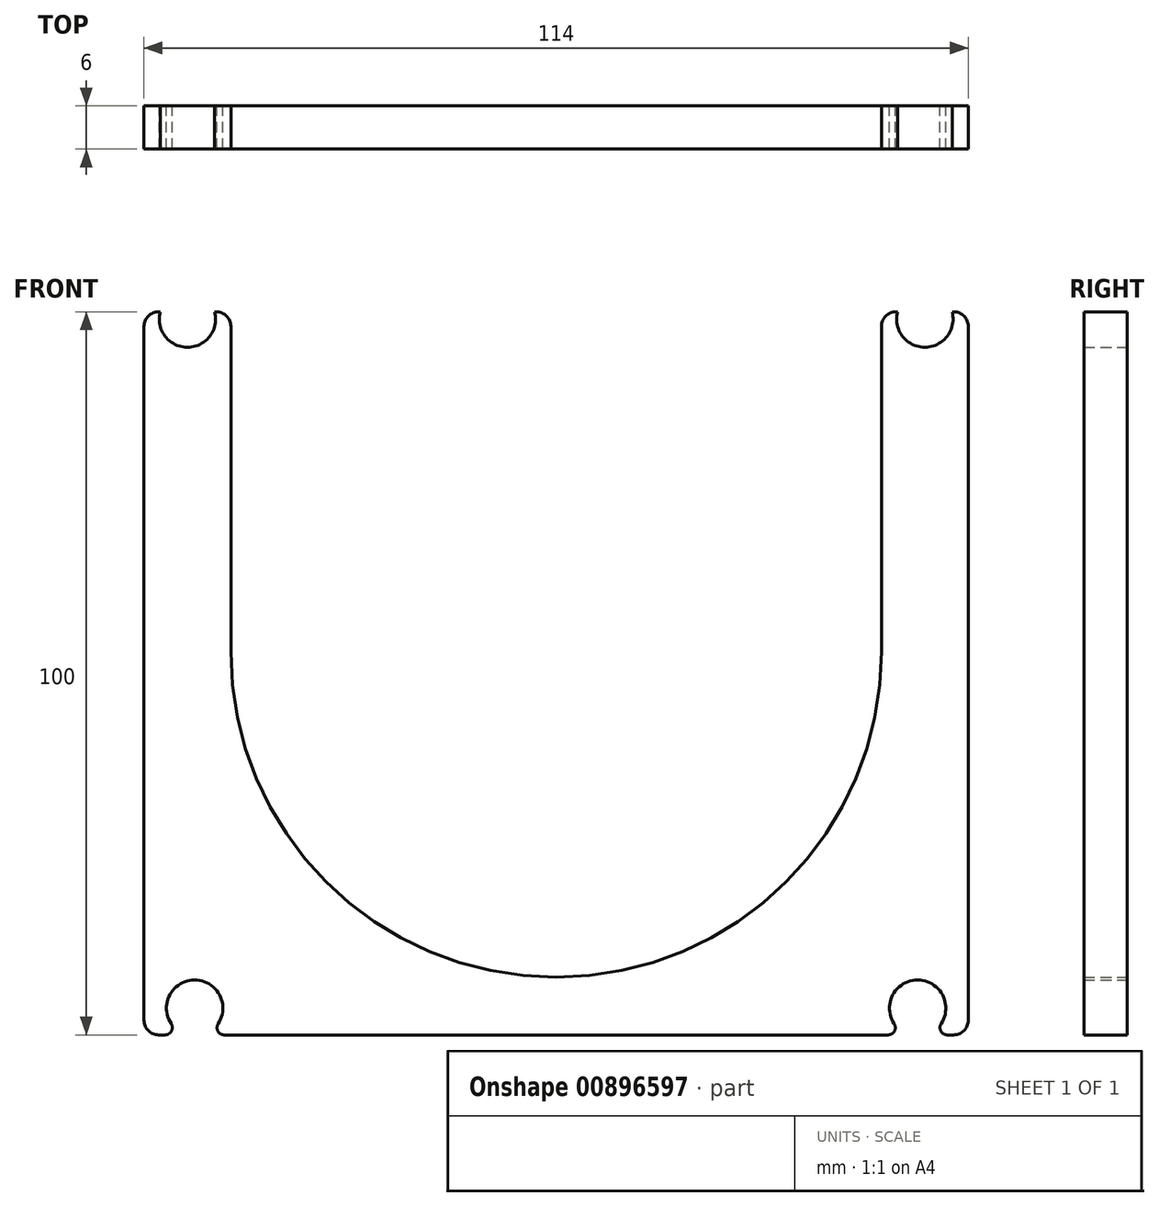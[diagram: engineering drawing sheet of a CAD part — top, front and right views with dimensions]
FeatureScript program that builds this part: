
annotation { "Feature Type Name" : "Feature", "Feature Type Description" : "" }
export const myFeature = defineFeature(function(context is Context, id is Id, definition is map)
    precondition{}
    {
        {
            var Q0;
            Q0=qCreatedBy(makeId("Front.planeOp"),FACE);
            var sketch = newSketch(context, id + "F0", { "sketchPlane" : qUnion([Q0])});
            skArc(sketch, "E0", {"start": v(-45, 53) * mm, "mid": v(0, 8) * mm, "end": v(45, 53) * mm});
            skLineSegment(sketch, "E1.bottom", {"start": v(-57, 100) * mm, "end": v(-54.77, 100) * mm});
            skLineSegment(sketch, "E1.top", {"start": v(-57, 0) * mm, "end": v(57, 0) * mm});
            skLineSegment(sketch, "E1.left", {"start": v(-57, 100) * mm, "end": v(-57, 0) * mm});
            skLineSegment(sketch, "E1.right", {"start": v(57, 100) * mm, "end": v(57, 0) * mm});
            skPoint(sketch, "E2", {"position": v(0, 0) * mm});
            skLineSegment(sketch, "E3", {"start": v(-45, 53) * mm, "end": v(-45, 100) * mm});
            skLineSegment(sketch, "E4.MirrorCS", {"start": v(45, 53) * mm, "end": v(45, 100) * mm});
            skLineSegment(sketch, "E5.trimOffspring", {"start": v(45, 100) * mm, "end": v(47.23, 100) * mm});
            skArc(sketch, "E6", {"start": v(47.23, 100) * mm, "mid": v(51, 95.1) * mm, "end": v(54.77, 100) * mm});
            skPoint(sketch, "E6.centerSnap0", {"position": v(51, 100) * mm});
            skLineSegment(sketch, "E7.trimOffspring", {"start": v(54.77, 100) * mm, "end": v(57, 100) * mm});
            skArc(sketch, "E8.MirrorCS", {"start": v(-47.23, 100) * mm, "mid": v(-51, 95.1) * mm, "end": v(-54.77, 100) * mm});
            skLineSegment(sketch, "E9.trimOffspring", {"start": v(-47.23, 100) * mm, "end": v(-45, 100) * mm});
            skSolve(sketch);
        }
        {
            var Q0;
            Q0 = qSketchRegion(id + "F0", true);
            extrude(context, id + "F1", {"entities" : qUnion([Q0]), "depth" : 6 * mm, "offsetDistance" : 25 * mm});
        }
        {
            var Q0;
            Q0=qCreatedBy(makeId("Front.planeOp"),FACE);
            var sketch = newSketch(context, id + "F2", { "sketchPlane" : qUnion([Q0])});
            skCircle(sketch, "E10", {"center": v(-50, 3.7) * mm, "radius": 3.9 * mm});
            skCircle(sketch, "E11.MirrorC", {"center": v(50, 3.7) * mm, "radius": 3.9 * mm});
            skSolve(sketch);
        }
        {
            var Q0;
            Q0 = qSketchRegion(id + "F2", true);
            extrude(context, id + "F3", {"entities" : qUnion([Q0]), "operationType" : NewBodyOperationType.REMOVE, "endBound" : BoundingType.THROUGH_ALL, "depth" : 25 * mm, "offsetDistance" : 25 * mm});
        }
        {
            var Q0;
            Q0=makeQuery(id+"F1.opExtrude","SWEPT_EDGE",EDGE,{"disambiguationData":[OSD([sQuery(id+"F0.wireOp",EDGE,"E3"),sQuery(id+"F0.wireOp",EDGE,"E9.trimOffspring")])]});
            var Q1;
            Q1=makeQuery(id+"F1.opExtrude","SWEPT_EDGE",EDGE,{"disambiguationData":[OSD([sQuery(id+"F0.wireOp",EDGE,"E4.MirrorCS"),sQuery(id+"F0.wireOp",EDGE,"E5.trimOffspring")])]});
            var Q2;
            Q2=makeQuery(id+"F1.opExtrude","SWEPT_EDGE",EDGE,{"disambiguationData":[OSD([sQuery(id+"F0.wireOp",EDGE,"E1.bottom"),sQuery(id+"F0.wireOp",EDGE,"E1.left")])]});
            var Q3;
            Q3=makeQuery(id+"F1.opExtrude","SWEPT_EDGE",EDGE,{"disambiguationData":[OSD([sQuery(id+"F0.wireOp",EDGE,"E1.right"),sQuery(id+"F0.wireOp",EDGE,"E7.trimOffspring")])]});
            var Q4;
            Q4=makeQuery(id+"F1.opExtrude","SWEPT_EDGE",EDGE,{"disambiguationData":[OSD([sQuery(id+"F0.wireOp",EDGE,"E1.top"),sQuery(id+"F0.wireOp",EDGE,"E1.right")])]});
            var Q5;
            Q5=makeQuery(id+"F1.opExtrude","SWEPT_EDGE",EDGE,{"disambiguationData":[OSD([sQuery(id+"F0.wireOp",EDGE,"E1.top"),sQuery(id+"F0.wireOp",EDGE,"E1.left")])]});
            fillet(context, id + "F4", {"entities" : qUnion([Q0, Q1, Q2, Q3, Q4, Q5]), "radius" : 2 * mm, "tangentPropagation" : true, "allowEdgeOverflow" : false});
        }
        {
            var Q0;
            Q0=makeQuery(id+"F3.boolean.opBoolean","INTERSECT",EDGE,{"disambiguationData":[OD(1.0)],"derivedFrom":[makeQuery(id+"F1.opExtrude","SWEPT_FACE",FACE,{"disambiguationData":[OSD([sQuery(id+"F0.wireOp",EDGE,"E1.top")])]}),makeQuery(id+"F3.opExtrude","SWEPT_FACE",FACE,{"disambiguationData":[OSD([sQuery(id+"F2.wireOp",EDGE,"E10")])]})]});
            var Q1;
            Q1=makeQuery(id+"F3.boolean.opBoolean","INTERSECT",EDGE,{"disambiguationData":[OD(0.0)],"derivedFrom":[makeQuery(id+"F1.opExtrude","SWEPT_FACE",FACE,{"disambiguationData":[OSD([sQuery(id+"F0.wireOp",EDGE,"E1.top")])]}),makeQuery(id+"F3.opExtrude","SWEPT_FACE",FACE,{"disambiguationData":[OSD([sQuery(id+"F2.wireOp",EDGE,"E10")])]})]});
            var Q2;
            Q2=makeQuery(id+"F3.boolean.opBoolean","INTERSECT",EDGE,{"disambiguationData":[OD(1.0)],"derivedFrom":[makeQuery(id+"F1.opExtrude","SWEPT_FACE",FACE,{"disambiguationData":[OSD([sQuery(id+"F0.wireOp",EDGE,"E1.top")])]}),makeQuery(id+"F3.opExtrude","SWEPT_FACE",FACE,{"disambiguationData":[OSD([sQuery(id+"F2.wireOp",EDGE,"E11.MirrorC")])]})]});
            var Q3;
            Q3=makeQuery(id+"F3.boolean.opBoolean","INTERSECT",EDGE,{"disambiguationData":[OD(0.0)],"derivedFrom":[makeQuery(id+"F1.opExtrude","SWEPT_FACE",FACE,{"disambiguationData":[OSD([sQuery(id+"F0.wireOp",EDGE,"E1.top")])]}),makeQuery(id+"F3.opExtrude","SWEPT_FACE",FACE,{"disambiguationData":[OSD([sQuery(id+"F2.wireOp",EDGE,"E11.MirrorC")])]})]});
            fillet(context, id + "F5", {"entities" : qUnion([Q0, Q1, Q2, Q3]), "radius" : 1 * mm, "tangentPropagation" : true, "allowEdgeOverflow" : false});
        }
    });
